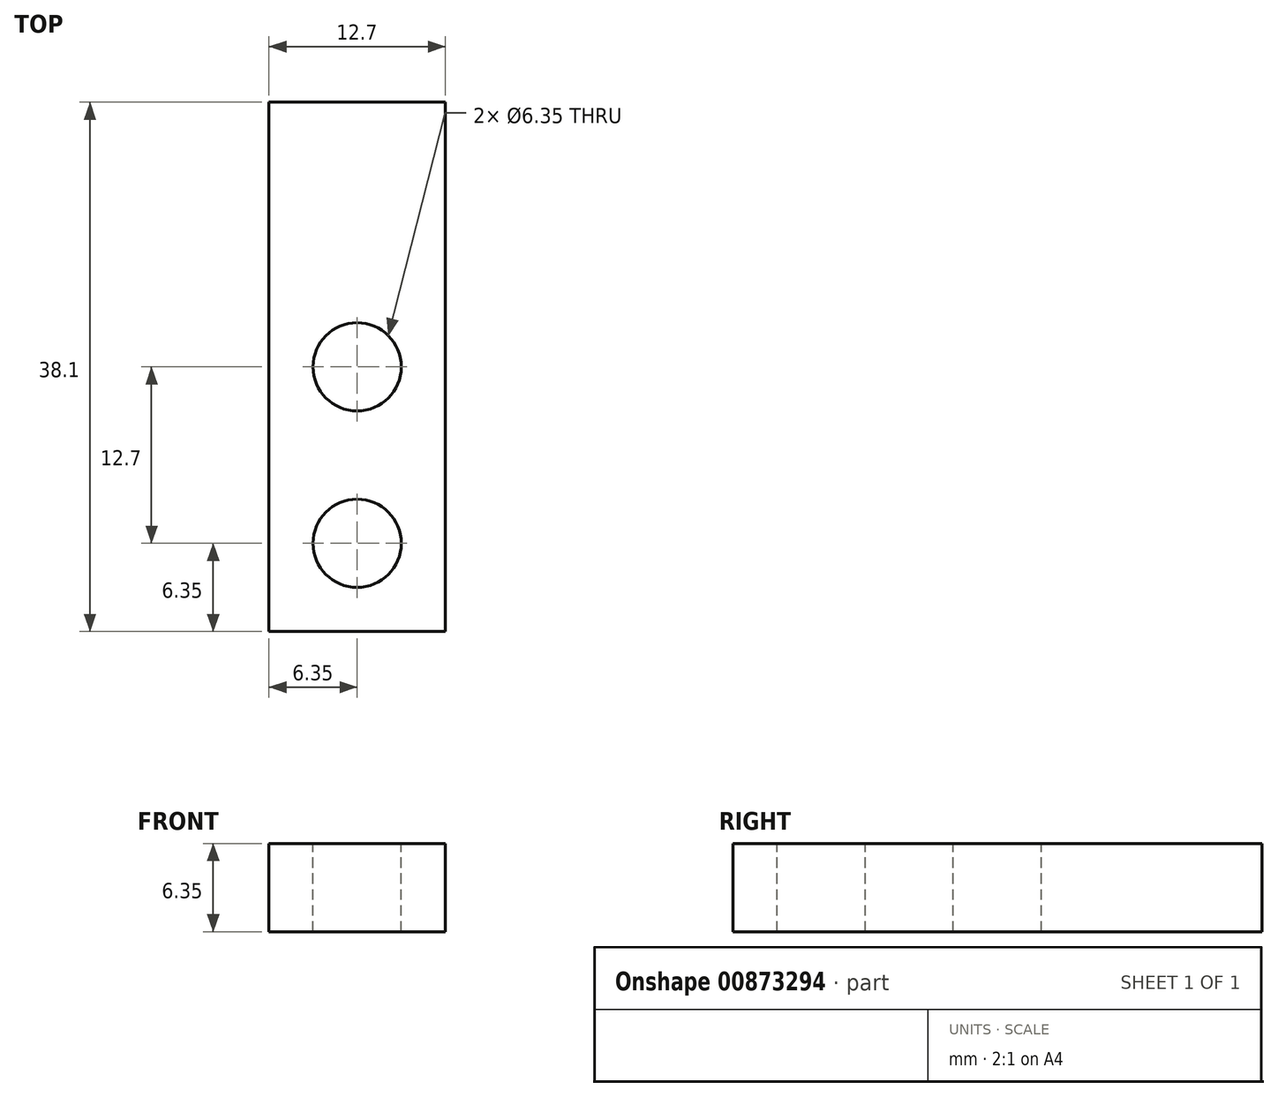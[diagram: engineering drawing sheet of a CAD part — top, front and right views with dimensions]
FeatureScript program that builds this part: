
annotation { "Feature Type Name" : "Feature", "Feature Type Description" : "" }
export const myFeature = defineFeature(function(context is Context, id is Id, definition is map)
    precondition{}
    {
        {
            var Q0;
            Q0=qCreatedBy(makeId("Front.planeOp"),FACE);
            var sketch = newSketch(context, id + "F0", { "sketchPlane" : qUnion([Q0])});
            skLineSegment(sketch, "E0.bottom", {"start": v(0, 0) * mm, "end": v(12.7, 0) * mm});
            skLineSegment(sketch, "E0.top", {"start": v(0, 6.35) * mm, "end": v(12.7, 6.35) * mm});
            skLineSegment(sketch, "E0.left", {"start": v(0, 0) * mm, "end": v(0, 6.35) * mm});
            skLineSegment(sketch, "E0.right", {"start": v(12.7, 0) * mm, "end": v(12.7, 6.35) * mm});
            skSolve(sketch);
        }
        {
            var Q0;
            Q0=makeQuery(id+"F0.imprint","IMPRINT",FACE,{"disambiguationData":[TD([[makeQuery(id+"F0.imprint","IMPRINT",EDGE,{"derivedFrom":sQuery(id+"F0.wireOp",EDGE,"E0.bottom")}),1.0]])]});
            extrude(context, id + "F1", {"entities" : qUnion([Q0]), "oppositeDirection" : true, "depth" : 38.1 * mm, "offsetDistance" : 25.4 * mm});
        }
        {
            var Q0;
            Q0=makeQuery(id+"F1.opExtrude","SWEPT_FACE",FACE,{"disambiguationData":[OSD([sQuery(id+"F0.wireOp",EDGE,"E0.top")])]});
            var sketch = newSketch(context, id + "F2", { "sketchPlane" : qUnion([Q0])});
            skCircle(sketch, "E1", {"center": v(6.35, 6.35) * mm, "radius": 3.18 * mm});
            skPoint(sketch, "E1.centerSnap0", {"position": v(6.35, 0) * mm});
            skCircle(sketch, "E2", {"center": v(6.35, 19.05) * mm, "radius": 3.18 * mm});
            skSolve(sketch);
        }
        {
            var Q0;
            Q0=makeQuery(id+"F2.imprint","IMPRINT",FACE,{"disambiguationData":[TD([[makeQuery(id+"F2.imprint","IMPRINT",EDGE,{"derivedFrom":sQuery(id+"F2.wireOp",EDGE,"E2")}),1.0]])]});
            var Q1;
            Q1=makeQuery(id+"F2.imprint","IMPRINT",FACE,{"disambiguationData":[TD([[makeQuery(id+"F2.imprint","IMPRINT",EDGE,{"derivedFrom":sQuery(id+"F2.wireOp",EDGE,"E1")}),1.0]])]});
            extrude(context, id + "F3", {"entities" : qUnion([Q0, Q1]), "operationType" : NewBodyOperationType.REMOVE, "endBound" : BoundingType.THROUGH_ALL, "oppositeDirection" : true, "depth" : 25.4 * mm, "offsetDistance" : 25.4 * mm});
        }
    });
